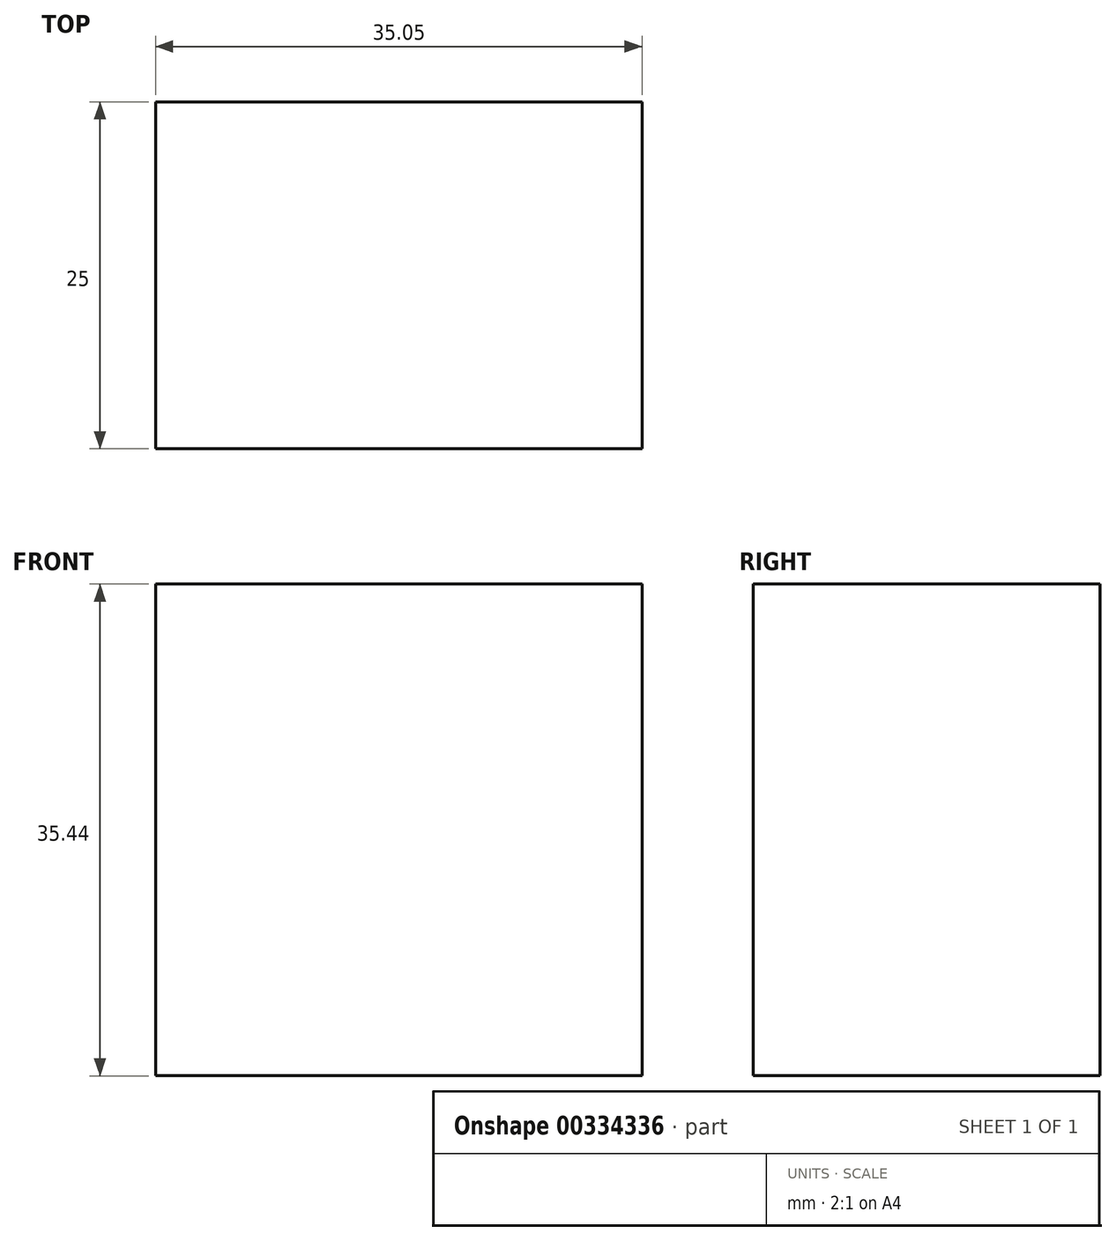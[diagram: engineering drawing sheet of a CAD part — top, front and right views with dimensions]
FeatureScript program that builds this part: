
annotation { "Feature Type Name" : "Feature", "Feature Type Description" : "" }
export const myFeature = defineFeature(function(context is Context, id is Id, definition is map)
    precondition{}
    {
        {
            var Q0;
            Q0=qCreatedBy(makeId("Front.planeOp"),FACE);
            var sketch = newSketch(context, id + "F0", { "sketchPlane" : qUnion([Q0])});
            skLineSegment(sketch, "E0.bottom", {"start": v(-83.41, 13.9) * mm, "end": v(-48.36, 13.9) * mm});
            skLineSegment(sketch, "E0.top", {"start": v(-83.41, 49.33) * mm, "end": v(-48.36, 49.33) * mm});
            skLineSegment(sketch, "E0.left", {"start": v(-83.41, 13.9) * mm, "end": v(-83.41, 49.33) * mm});
            skLineSegment(sketch, "E0.right", {"start": v(-48.36, 13.9) * mm, "end": v(-48.36, 49.33) * mm});
            skPoint(sketch, "E0.middle", {"position": v(-65.89, 31.61) * mm});
            skSolve(sketch);
        }
        {
            var Q0;
            Q0=makeQuery(id+"F0.imprint","IMPRINT",FACE,{"disambiguationData":[TD([[makeQuery(id+"F0.imprint","IMPRINT",EDGE,{"derivedFrom":sQuery(id+"F0.wireOp",EDGE,"E0.bottom")}),1.0]])]});
            extrude(context, id + "F1", {"entities" : qUnion([Q0]), "depth" : 25 * mm});
        }
    });
